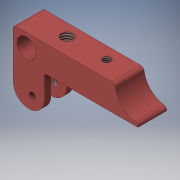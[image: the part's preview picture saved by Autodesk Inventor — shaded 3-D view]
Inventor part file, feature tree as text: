
AUTODESK INVENTOR PART (.ipt)
format: ipt  version: 2016 SP1 (Build 200210100, 210)  size: 147,456 bytes
history: native  units: mm
features: sketch x7, other x3
ambient origin geometry x8: Origin, YZ Plane, XZ Plane, XY Plane, X Axis, Y Axis, Z Axis, Center Point
bodies: Solid1 (feature_tree)
feature tree (10):
  other  "Part2.ipt"
  other  "Solid1::Part2.ipt"
  other  "TaggingFeature1"
  sketch  "Sketch1"  dims[d0=10.0mm]
  sketch  "Sketch2"
  sketch  "Sketch3"
  sketch  "Sketch4"
  sketch  "Sketch5"
  sketch  "Sketch6"
  sketch  "Sketch7"
